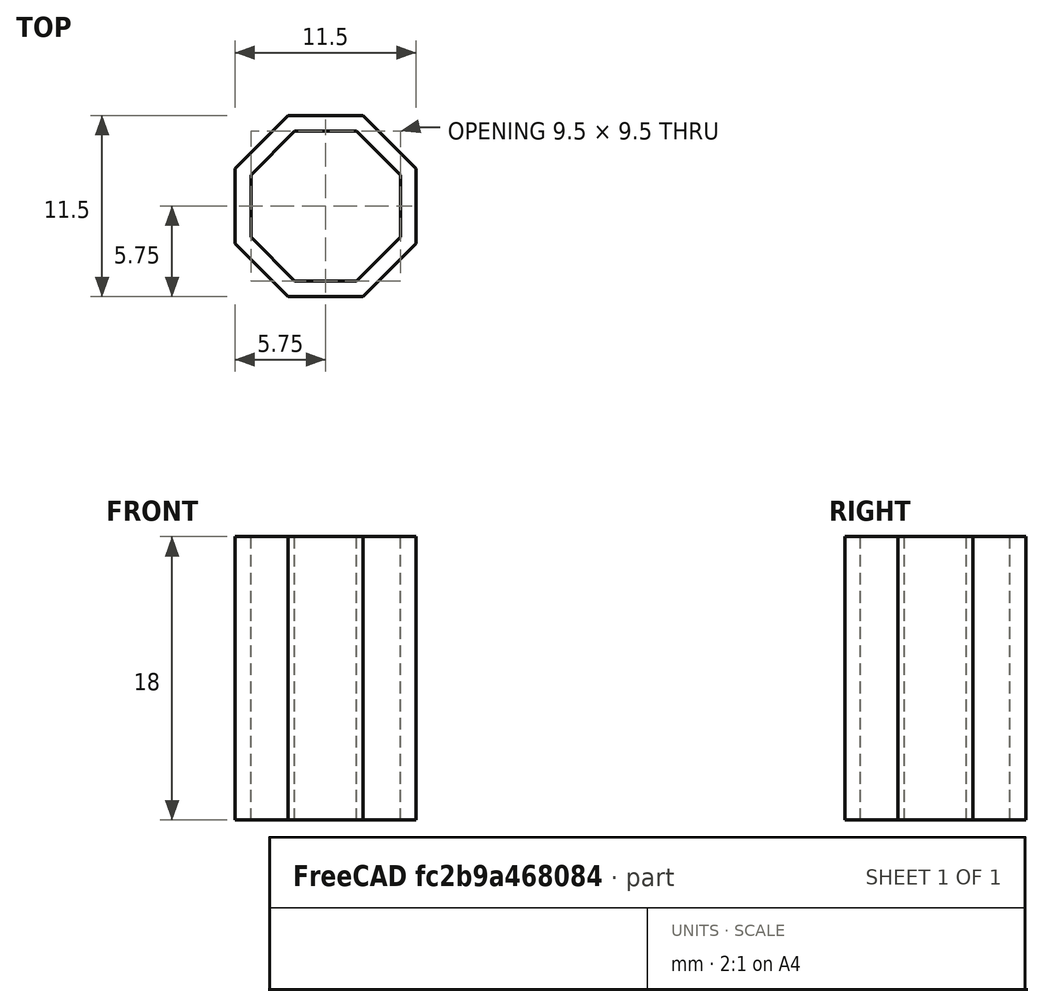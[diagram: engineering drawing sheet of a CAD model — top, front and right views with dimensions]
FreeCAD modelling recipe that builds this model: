
FCSTD DOCUMENT  (FreeCAD 0.21R33771 (Git))
Label: color_marker_for_mini_jack_plug
License: All rights reserved
LicenseURL: https://en.wikipedia.org/wiki/All_rights_reserved
objects: Sketcher::SketchObject×1, PartDesign::Pad×1, PartDesign::Body×1
note: 4 computed .brp shape members not serialized (recipe doc carries the construction recipe); baked Part::Feature solids carry a one-line shape summary decoded from their .brp

FEATURE [Sketcher::SketchObject] Sketch
  FullyConstrained = true
  MapMode = 5
  Support = -> [XY_Plane]
  sketch-geometry (18):
    g0: LineSegment StartX=1.96751 StartY=4.75 StartZ=0 EndX=-1.96751 EndY=4.75 EndZ=0
    g1: LineSegment StartX=-1.96751 StartY=4.75 StartZ=0 EndX=-4.75 EndY=1.96751 EndZ=0
    g2: LineSegment StartX=-4.75 StartY=1.96751 StartZ=0 EndX=-4.75 EndY=-1.96751 EndZ=0
    g3: LineSegment StartX=-4.75 StartY=-1.96751 StartZ=0 EndX=-1.96751 EndY=-4.75 EndZ=0
    g4: LineSegment StartX=-1.96751 StartY=-4.75 StartZ=0 EndX=1.96751 EndY=-4.75 EndZ=0
    g5: LineSegment StartX=1.96751 StartY=-4.75 StartZ=0 EndX=4.75 EndY=-1.96751 EndZ=0
    g6: LineSegment StartX=4.75 StartY=-1.96751 StartZ=0 EndX=4.75 EndY=1.96751 EndZ=0
    g7: LineSegment StartX=4.75 StartY=1.96751 StartZ=0 EndX=1.96751 EndY=4.75 EndZ=0
    g8: Circle CenterX=0 CenterY=0 CenterZ=0 NormalX=0 NormalY=0 NormalZ=1 AngleXU=0 Radius=5.14136
    g9: LineSegment StartX=5.75 StartY=2.38173 StartZ=0 EndX=2.38173 EndY=5.75 EndZ=0
    g10: LineSegment StartX=2.38173 StartY=5.75 StartZ=0 EndX=-2.38173 EndY=5.75 EndZ=0
    g11: LineSegment StartX=-2.38173 StartY=5.75 StartZ=0 EndX=-5.75 EndY=2.38173 EndZ=0
    g12: LineSegment StartX=-5.75 StartY=2.38173 StartZ=0 EndX=-5.75 EndY=-2.38173 EndZ=0
    g13: LineSegment StartX=-5.75 StartY=-2.38173 StartZ=0 EndX=-2.38173 EndY=-5.75 EndZ=0
    g14: LineSegment StartX=-2.38173 StartY=-5.75 StartZ=0 EndX=2.38173 EndY=-5.75 EndZ=0
    g15: LineSegment StartX=2.38173 StartY=-5.75 StartZ=0 EndX=5.75 EndY=-2.38173 EndZ=0
    g16: LineSegment StartX=5.75 StartY=-2.38173 StartZ=0 EndX=5.75 EndY=2.38173 EndZ=0
    g17: Circle CenterX=0 CenterY=0 CenterZ=0 NormalX=0 NormalY=0 NormalZ=1 AngleXU=0 Radius=6.22376
  constraints (40):
    c: Coincident(g0,g1)
    c: Coincident(g1,g2)
    c: Coincident(g2,g3)
    c: Coincident(g3,g4)
    c: Coincident(g4,g5)
    c: Coincident(g5,g6)
    c: Coincident(g6,g7)
    c: Coincident(g7,g0)
    c: Equal(g0, g1-g7) x7
    c: PointOnObject(g0,g8)
    c: PointOnObject(g1,g8)
    c: PointOnObject(g2,g8)
    c: PointOnObject(g3,g8)
    c: PointOnObject(g4,g8)
    c: PointOnObject(g5,g8)
    c: PointOnObject(g6,g8)
    c: PointOnObject(g7,g8)
    c: Coincident(g8,g-1)
    c: Horizontal(g0)
    c: DistanceX(g1,g6) = 9.5
    c: Coincident(g9,g10)
    c: Coincident(g10,g11)
    c: Coincident(g11,g12)
    c: Coincident(g12,g13)
    c: Coincident(g13,g14)
    c: Coincident(g14,g15)
    c: Coincident(g15,g16)
    c: Coincident(g16,g9)
    c: Equal(g9, g10-g16) x7
    c: PointOnObject(g9,g17)
    c: PointOnObject(g10,g17)
    c: PointOnObject(g11,g17)
    c: PointOnObject(g12,g17)
    c: PointOnObject(g13,g17)
    c: PointOnObject(g14,g17)
    c: PointOnObject(g15,g17)
    c: PointOnObject(g16,g17)
    c: Coincident(g17,g8)
    c: Horizontal(g10)
    c: DistanceY(g0,g9) = 1
FEATURE [PartDesign::Pad] Pad
  Direction = (0,0,1)
  Length = 18
  Length2 = 10
  Profile = -> Sketch
  ReferenceAxis = -> Sketch [N_Axis]
  Type = 0
FEATURE [PartDesign::Body] Body
  Group = -> [Sketch,Pad]
  Origin = -> Origin
  Tip = -> Pad
